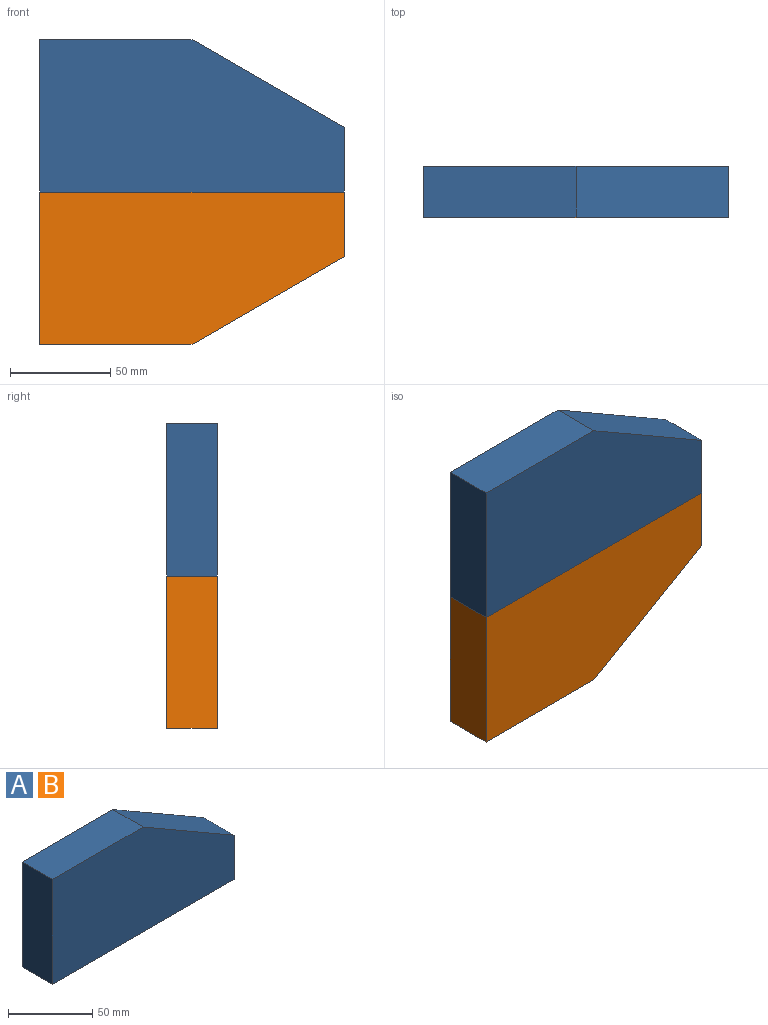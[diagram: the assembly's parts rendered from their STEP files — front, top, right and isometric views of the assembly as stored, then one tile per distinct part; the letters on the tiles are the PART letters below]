
ASSEMBLY  parts=2 mates=1
PART A: 7 faces, bbox 152.4x25.4x76.2 mm
  f0: plane 76.2x25.4mm, normal (-1,0,0), area 1935.5mm2, adj f1,f4,f5,f6
  f1: plane 152.4x25.4mm, normal (0,0,-1), area 3871mm2, adj f0,f2,f5,f6
  f2: plane 32.21x25.4mm, normal (1,0,0), area 818mm2, adj f1,f3,f5,f6
  f3: plane 76.2x43.99mm, normal (0.5,0,0.87), area 2234.9mm2, adj f2,f4,f5,f6
  f4: plane 76.2x25.4mm, normal (0,0,1), area 1935.5mm2, adj f0,f3,f5,f6
  f5: plane 152.4x76.2mm, normal (0,-1,0), area 9936.7mm2, adj f0,f1,f2,f3,f4
  f6: plane 152.4x76.2mm, normal (0,1,0), area 9936.7mm2, adj f0,f1,f2,f3,f4
PART B: same geometry as A
PLACE A t=(-9.07,68.11,-13.12)mm fixed
PLACE B rot(axis=(1,0,0),180deg) t=(-9.07,42.71,-13.12)mm
MATE fastened B.f6 <-> A.f5  axis (0,-1,0) through (67.13,42.71,-13.12)mm
